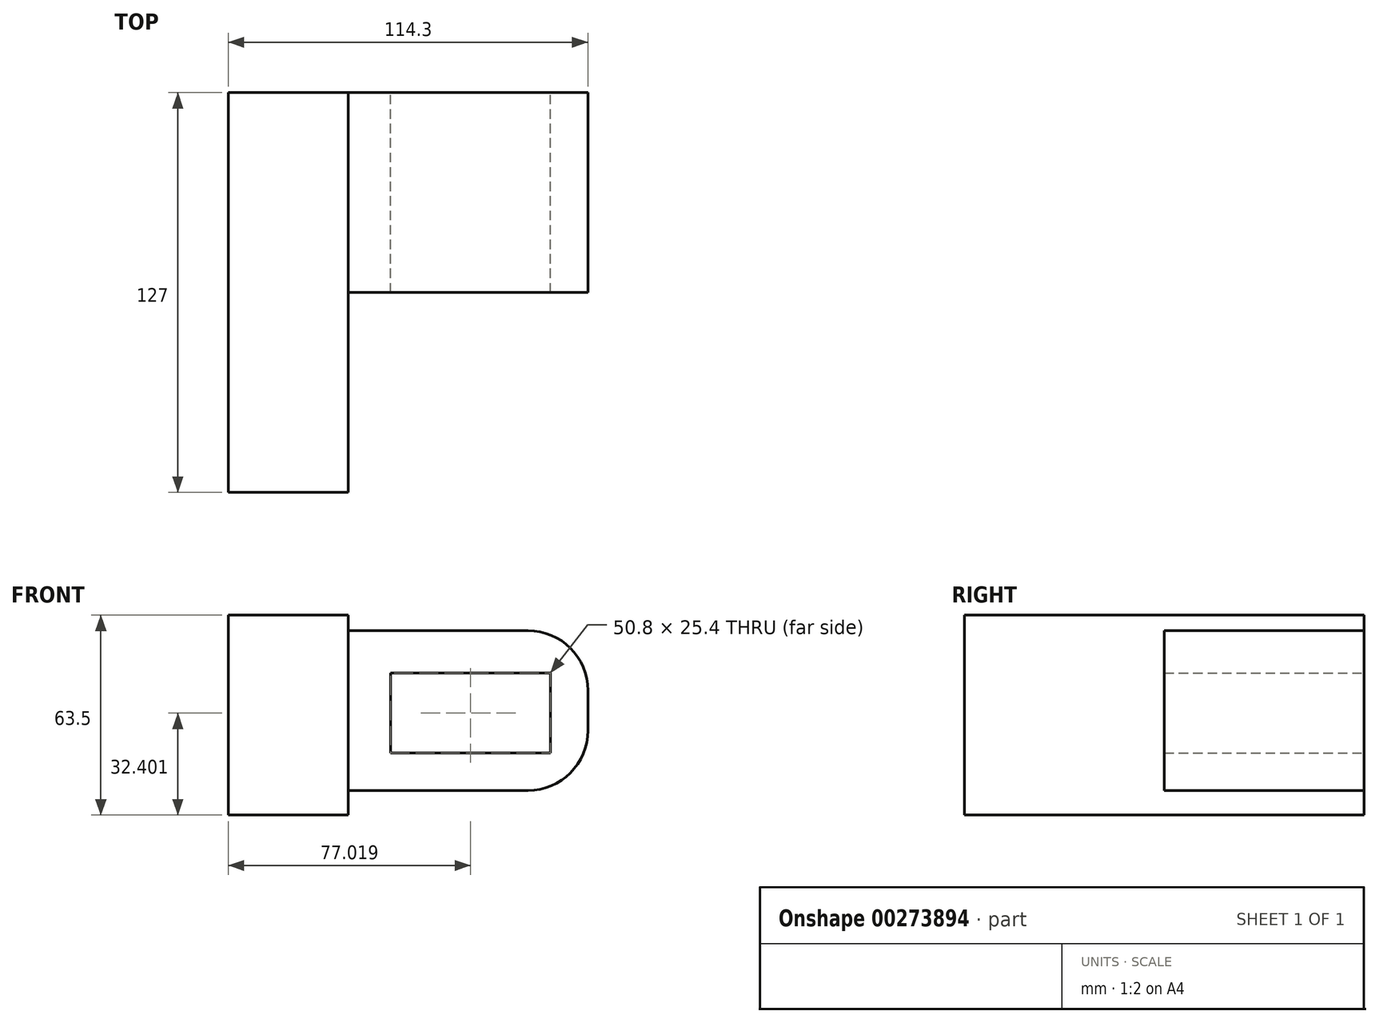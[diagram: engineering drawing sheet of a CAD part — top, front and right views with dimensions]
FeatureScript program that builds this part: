
annotation { "Feature Type Name" : "Feature", "Feature Type Description" : "" }
export const myFeature = defineFeature(function(context is Context, id is Id, definition is map)
    precondition{}
    {
        {
            var Q0;
            Q0=qCreatedBy(makeId("Front.planeOp"),FACE);
            var sketch = newSketch(context, id + "F0", { "sketchPlane" : qUnion([Q0])});
            skLineSegment(sketch, "E0.bottom", {"start": v(38.1, -25.4) * mm, "end": v(-38.1, -25.4) * mm});
            skLineSegment(sketch, "E0.top", {"start": v(38.1, 25.4) * mm, "end": v(-38.1, 25.4) * mm});
            skLineSegment(sketch, "E0.left", {"start": v(38.1, -25.4) * mm, "end": v(38.1, 25.4) * mm});
            skLineSegment(sketch, "E0.right", {"start": v(-38.1, -25.4) * mm, "end": v(-38.1, 25.4) * mm});
            skPoint(sketch, "E0.middle", {"position": v(0, 0) * mm});
            skLineSegment(sketch, "E1.bottom", {"start": v(-24.58, 11.88) * mm, "end": v(26.22, 11.88) * mm});
            skLineSegment(sketch, "E1.top", {"start": v(-24.58, -13.52) * mm, "end": v(26.22, -13.52) * mm});
            skLineSegment(sketch, "E1.left", {"start": v(-24.58, 11.88) * mm, "end": v(-24.58, -13.52) * mm});
            skLineSegment(sketch, "E1.right", {"start": v(26.22, 11.88) * mm, "end": v(26.22, -13.52) * mm});
            skSolve(sketch);
        }
        {
            var Q0;
            Q0=makeQuery(id+"F0.imprint","IMPRINT",FACE,{"disambiguationData":[TD([[makeQuery(id+"F0.imprint","IMPRINT",EDGE,{"derivedFrom":sQuery(id+"F0.wireOp",EDGE,"E0.bottom")}),-1.0]])]});
            extrude(context, id + "F1", {"entities" : qUnion([Q0]), "depth" : 63.5 * mm});
        }
        {
            var Q0;
            Q0=makeQuery(id+"F1.opExtrude","SWEPT_EDGE",EDGE,{"disambiguationData":[OSD([sQuery(id+"F0.wireOp",EDGE,"E0.top"),sQuery(id+"F0.wireOp",EDGE,"E0.left")])]});
            var Q1;
            Q1=makeQuery(id+"F1.opExtrude","SWEPT_EDGE",EDGE,{"disambiguationData":[OSD([sQuery(id+"F0.wireOp",EDGE,"E0.bottom"),sQuery(id+"F0.wireOp",EDGE,"E0.left")])]});
            fillet(context, id + "F2", {"entities" : qUnion([Q0, Q1]), "radius" : 19.05 * mm, "tangentPropagation" : true, "allowEdgeOverflow" : false});
        }
        {
            var Q0;
            Q0=qCreatedBy(makeId("Front.planeOp"),FACE);
            var sketch = newSketch(context, id + "F3", { "sketchPlane" : qUnion([Q0])});
            skLineSegment(sketch, "E2.bottom", {"start": v(-38.1, -33.22) * mm, "end": v(-76.2, -33.22) * mm});
            skLineSegment(sketch, "E2.top", {"start": v(-38.1, 30.28) * mm, "end": v(-76.2, 30.28) * mm});
            skLineSegment(sketch, "E2.left", {"start": v(-38.1, -33.22) * mm, "end": v(-38.1, 30.28) * mm});
            skLineSegment(sketch, "E2.right", {"start": v(-76.2, -33.22) * mm, "end": v(-76.2, 30.28) * mm});
            skLineSegment(sketch, "E3", {"start": v(-38.1, 30.28) * mm, "end": v(-38.1, -33.22) * mm});
            skSolve(sketch);
        }
        {
            var Q0;
            Q0=makeQuery(id+"F3.imprint","IMPRINT",FACE,{"disambiguationData":[TD([[makeQuery(id+"F3.imprint","IMPRINT",EDGE,{"derivedFrom":sQuery(id+"F3.wireOp",EDGE,"E2.bottom")}),-1.0]])]});
            extrude(context, id + "F4", {"entities" : qUnion([Q0]), "operationType" : NewBodyOperationType.ADD, "depth" : 127 * mm});
        }
    });
